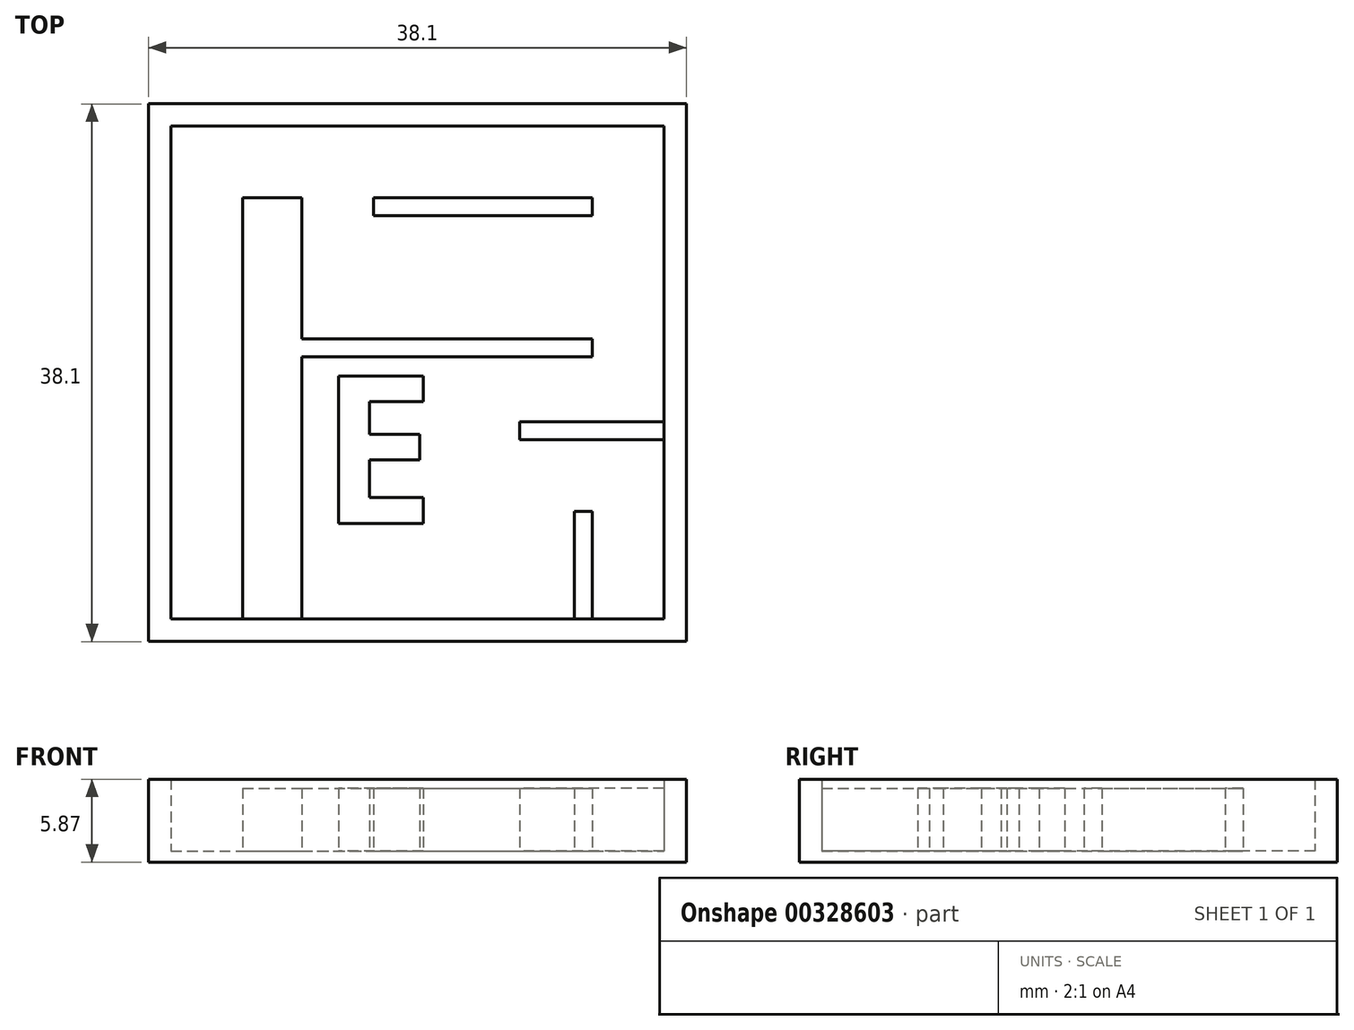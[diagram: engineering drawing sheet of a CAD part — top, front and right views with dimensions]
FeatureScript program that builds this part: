
annotation { "Feature Type Name" : "Feature", "Feature Type Description" : "" }
export const myFeature = defineFeature(function(context is Context, id is Id, definition is map)
    precondition{}
    {
        {
            var Q0;
            Q0=qCreatedBy(makeId("Top.planeOp"),FACE);
            var sketch = newSketch(context, id + "F0", { "sketchPlane" : qUnion([Q0])});
            skLineSegment(sketch, "E0.bottom", {"start": v(-22.75, 18.51) * mm, "end": v(15.35, 18.51) * mm});
            skLineSegment(sketch, "E0.top", {"start": v(-22.75, -19.59) * mm, "end": v(15.35, -19.59) * mm});
            skLineSegment(sketch, "E0.left", {"start": v(-22.75, 18.51) * mm, "end": v(-22.75, -19.59) * mm});
            skLineSegment(sketch, "E0.right", {"start": v(15.35, 18.51) * mm, "end": v(15.35, -19.59) * mm});
            skSolve(sketch);
        }
        {
            var Q0;
            Q0=makeQuery(id+"F0.imprint","IMPRINT",FACE,{"disambiguationData":[TD([[makeQuery(id+"F0.imprint","IMPRINT",EDGE,{"derivedFrom":sQuery(id+"F0.wireOp",EDGE,"E0.bottom")}),-1.0]])]});
            extrude(context, id + "F1", {"entities" : qUnion([Q0]), "depth" : 0.8 * mm});
        }
        {
            var Q0;
            Q0=makeQuery(id+"F1.opExtrude","CAP_FACE",FACE,{"disambiguationData":[OSD([sQuery(id+"F0.wireOp",EDGE,"E0.bottom"),sQuery(id+"F0.wireOp",EDGE,"E0.top"),sQuery(id+"F0.wireOp",EDGE,"E0.left"),sQuery(id+"F0.wireOp",EDGE,"E0.right")])],"isStart":false});
            var sketch = newSketch(context, id + "F2", { "sketchPlane" : qUnion([Q0])});
            skLineSegment(sketch, "E1.0", {"start": v(-21.16, 16.93) * mm, "end": v(13.76, 16.93) * mm});
            skLineSegment(sketch, "E1.1", {"start": v(-21.16, 16.93) * mm, "end": v(-21.16, -18) * mm});
            skLineSegment(sketch, "E1.2", {"start": v(-21.16, -18) * mm, "end": v(13.76, -18) * mm});
            skLineSegment(sketch, "E1.3", {"start": v(13.76, 16.93) * mm, "end": v(13.76, -18) * mm});
            skSolve(sketch);
        }
        {
            var Q0;
            Q0=makeQuery(id+"F2.imprint","IMPRINT",FACE,{"disambiguationData":[TD([[makeQuery(id+"F2.imprint","IMPRINT",EDGE,{"derivedFrom":sQuery(id+"F2.wireOp",EDGE,"E1.0")}),1.0]])]});
            extrude(context, id + "F3", {"entities" : qUnion([Q0]), "operationType" : NewBodyOperationType.ADD, "depth" : 5.08 * mm});
        }
        {
            var Q0;
            Q0=makeQuery(id+"F1.opExtrude","CAP_FACE",FACE,{"disambiguationData":[OSD([sQuery(id+"F0.wireOp",EDGE,"E0.bottom"),sQuery(id+"F0.wireOp",EDGE,"E0.top"),sQuery(id+"F0.wireOp",EDGE,"E0.left"),sQuery(id+"F0.wireOp",EDGE,"E0.right")])],"isStart":false});
            var sketch = newSketch(context, id + "F4", { "sketchPlane" : qUnion([Q0])});
            skLineSegment(sketch, "E2.bottom", {"start": v(-16.08, -18) * mm, "end": v(-11.88, -18) * mm});
            skLineSegment(sketch, "E2.top", {"start": v(-16.08, 11.85) * mm, "end": v(-11.88, 11.85) * mm});
            skLineSegment(sketch, "E2.left", {"start": v(-16.08, -18) * mm, "end": v(-16.08, 11.85) * mm});
            skLineSegment(sketch, "E2.right", {"start": v(-11.88, -18) * mm, "end": v(-11.88, 0.58) * mm});
            skLineSegment(sketch, "E3.bottom", {"start": v(7.41, -18) * mm, "end": v(8.68, -18) * mm});
            skLineSegment(sketch, "E3.top", {"start": v(7.41, -10.38) * mm, "end": v(8.68, -10.38) * mm});
            skLineSegment(sketch, "E3.left", {"start": v(7.41, -18) * mm, "end": v(7.41, -10.38) * mm});
            skLineSegment(sketch, "E3.right", {"start": v(8.68, -18) * mm, "end": v(8.68, -10.38) * mm});
            skLineSegment(sketch, "E4.bottom", {"start": v(13.76, -4.03) * mm, "end": v(3.54, -4.03) * mm});
            skLineSegment(sketch, "E4.top", {"start": v(13.76, -5.3) * mm, "end": v(3.54, -5.3) * mm});
            skLineSegment(sketch, "E4.left", {"start": v(13.76, -4.03) * mm, "end": v(13.76, -5.3) * mm});
            skLineSegment(sketch, "E4.right", {"start": v(3.54, -4.03) * mm, "end": v(3.54, -5.3) * mm});
            skLineSegment(sketch, "E5.bottom", {"start": v(-6.8, 11.85) * mm, "end": v(8.68, 11.85) * mm});
            skLineSegment(sketch, "E5.top", {"start": v(-6.8, 10.58) * mm, "end": v(8.68, 10.58) * mm});
            skLineSegment(sketch, "E5.left", {"start": v(-6.8, 11.85) * mm, "end": v(-6.8, 10.58) * mm});
            skLineSegment(sketch, "E5.right", {"start": v(8.68, 11.85) * mm, "end": v(8.68, 10.58) * mm});
            skLineSegment(sketch, "E6.bottom", {"start": v(-11.88, 1.85) * mm, "end": v(8.68, 1.85) * mm});
            skLineSegment(sketch, "E6.top", {"start": v(-11.88, 0.58) * mm, "end": v(8.68, 0.58) * mm});
            skLineSegment(sketch, "E6.right", {"start": v(8.68, 1.85) * mm, "end": v(8.68, 0.58) * mm});
            skCircle(sketch, "E7", {"center": v(-18.7, -15.35) * mm, "radius": 1.27 * mm});
            skCircle(sketch, "E8", {"center": v(11.16, -15.42) * mm, "radius": 1.27 * mm});
            skText(sketch, "E9", { "text": "E", "fontName": "OpenSans-Bold.ttf"});
            skLineSegment(sketch, "E10.trimOffspring", {"start": v(-11.88, 1.85) * mm, "end": v(-11.88, 11.85) * mm});
            const initialGuessF4  = {"E9": [-0.01061, -0.01122, 1, 0, 0.01052]};
            skSetInitialGuess(sketch, initialGuessF4);
            skSolve(sketch);
        }
        {
            var Q0;
            Q0=makeQuery(id+"F4.imprint","IMPRINT",FACE,{"disambiguationData":[TD([[makeQuery(id+"F4.imprint","IMPRINT",EDGE,{"derivedFrom":sQuery(id+"F4.wireOp",EDGE,"E9.sketch_text.stroke-0")}),-1.0]])]});
            var Q1;
            Q1=makeQuery(id+"F4.imprint","IMPRINT",FACE,{"disambiguationData":[TD([[makeQuery(id+"F4.imprint","IMPRINT",EDGE,{"derivedFrom":sQuery(id+"F4.wireOp",EDGE,"E2.bottom")}),1.0]])]});
            var Q2;
            Q2=makeQuery(id+"F4.imprint","IMPRINT",FACE,{"disambiguationData":[TD([[makeQuery(id+"F4.imprint","IMPRINT",EDGE,{"derivedFrom":sQuery(id+"F4.wireOp",EDGE,"E5.bottom")}),-1.0]])]});
            var Q3;
            Q3=makeQuery(id+"F4.imprint","IMPRINT",FACE,{"disambiguationData":[TD([[makeQuery(id+"F4.imprint","IMPRINT",EDGE,{"derivedFrom":sQuery(id+"F4.wireOp",EDGE,"E4.bottom")}),1.0]])]});
            var Q4;
            Q4=makeQuery(id+"F4.imprint","IMPRINT",FACE,{"disambiguationData":[TD([[makeQuery(id+"F4.imprint","IMPRINT",EDGE,{"derivedFrom":sQuery(id+"F4.wireOp",EDGE,"E3.bottom")}),1.0]])]});
            extrude(context, id + "F5", {"entities" : qUnion([Q0, Q1, Q2, Q3, Q4]), "operationType" : NewBodyOperationType.ADD, "depth" : 4.44 * mm});
        }
    });
